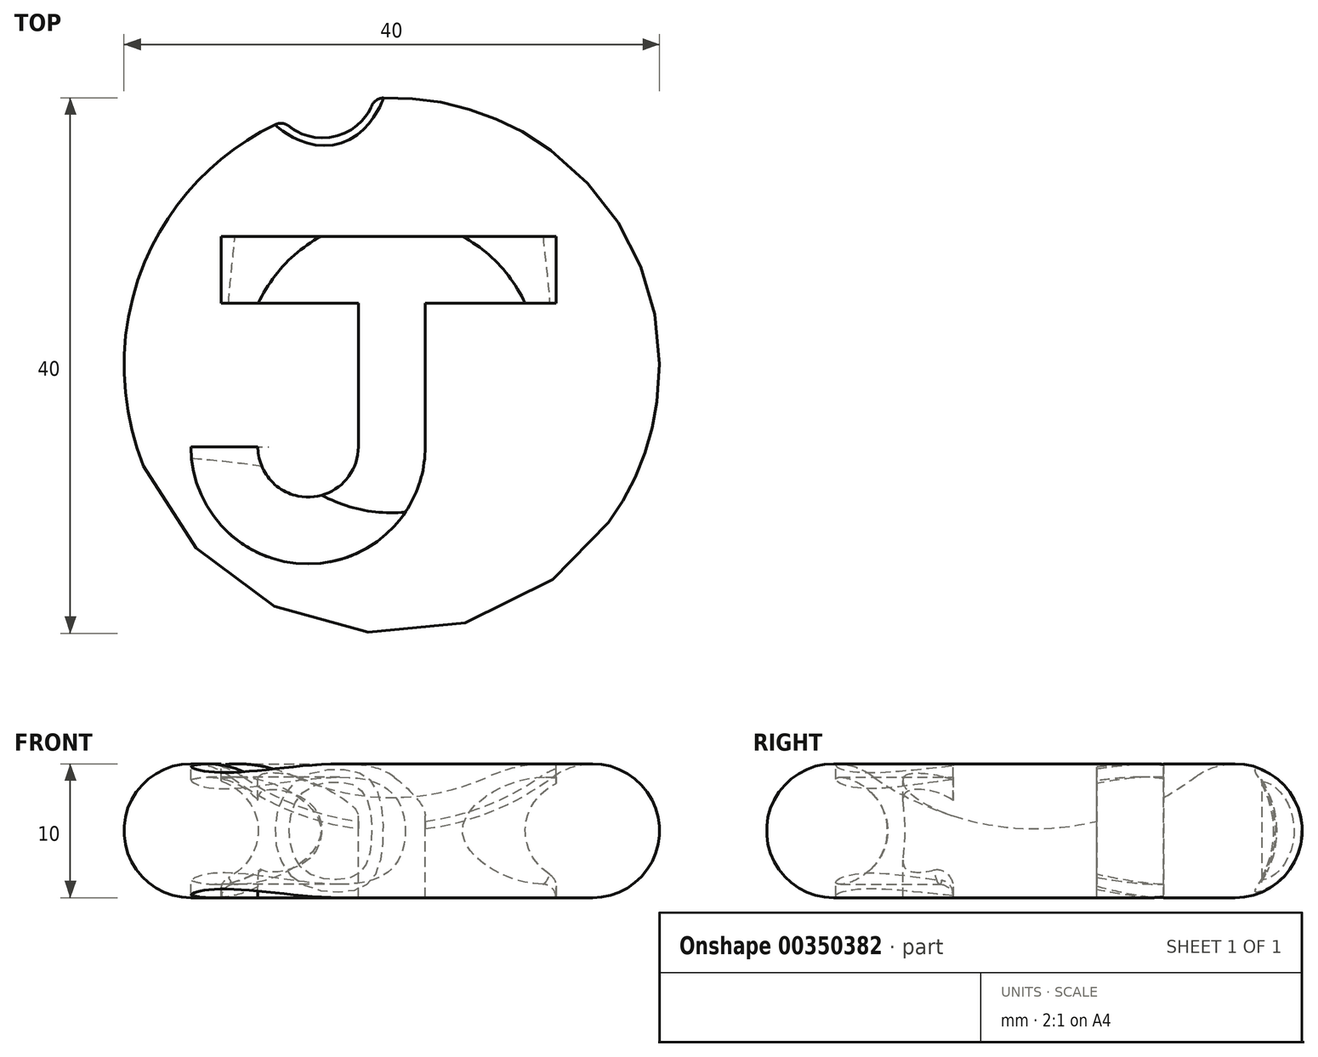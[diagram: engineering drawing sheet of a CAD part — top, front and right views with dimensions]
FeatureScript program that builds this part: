
annotation { "Feature Type Name" : "Feature", "Feature Type Description" : "" }
export const myFeature = defineFeature(function(context is Context, id is Id, definition is map)
    precondition{}
    {
        {
            var Q0;
            Q0=qCreatedBy(makeId("Front.planeOp"),FACE);
            var sketch = newSketch(context, id + "F0", { "sketchPlane" : qUnion([Q0])});
            skArc(sketch, "E0", {"start": v(-12, 9) * mm, "mid": v(-19.74, 6.58) * mm, "end": v(-15, 0) * mm});
            skArc(sketch, "E1", {"start": v(-12, 9) * mm, "mid": v(-6.32, 6.03) * mm, "end": v(0, 5) * mm});
            skLineSegment(sketch, "E2", {"start": v(-15, 0) * mm, "end": v(0, 0) * mm});
            skLineSegment(sketch, "E3", {"start": v(0, 0) * mm, "end": v(0, 5) * mm});
            skPoint(sketch, "E4.orphan", {"position": v(-50.33, 0) * mm});
            skSolve(sketch);
        }
        {
            var Q0;
            Q0=qCreatedBy(makeId("Top.planeOp"),FACE);
            cPlane(context, id + "F1", {"entities" : qUnion([Q0]), "cplaneType" : CPlaneType.OFFSET, "offset" : 10 * mm, "width" : 150 * mm, "height" : 150 * mm});
        }
        {
            var Q0;
            Q0=qCreatedBy(id+"F1.planeOp",FACE);
            var sketch = newSketch(context, id + "F2", { "sketchPlane" : qUnion([Q0])});
            skLineSegment(sketch, "E5", {"start": v(-12.74, 9.65) * mm, "end": v(12.26, 9.65) * mm});
            skLineSegment(sketch, "E6", {"start": v(-12.74, 4.65) * mm, "end": v(-2.5, 4.65) * mm});
            skArc(sketch, "E7", {"start": v(-15, -6.07) * mm, "mid": v(-6.25, -14.82) * mm, "end": v(2.5, -6.07) * mm});
            skLineSegment(sketch, "E8.0", {"start": v(2.5, 4.65) * mm, "end": v(2.5, -6.07) * mm});
            skLineSegment(sketch, "E9.0", {"start": v(-2.5, 4.65) * mm, "end": v(-2.5, -6.07) * mm});
            skLineSegment(sketch, "E10", {"start": v(-15, -6.07) * mm, "end": v(-10, -6.07) * mm});
            skArc(sketch, "E11", {"start": v(-10, -6.07) * mm, "mid": v(-6.25, -9.82) * mm, "end": v(-2.5, -6.07) * mm});
            skLineSegment(sketch, "E12.trimOffspring", {"start": v(2.5, 4.65) * mm, "end": v(12.26, 4.65) * mm});
            skLineSegment(sketch, "E13.trimOffspring", {"start": v(-2.5, -13.98) * mm, "end": v(-2.5, -14.03) * mm});
            skLineSegment(sketch, "E14.0", {"start": v(-12.74, 9.65) * mm, "end": v(-12.74, 4.65) * mm});
            skLineSegment(sketch, "E15.0", {"start": v(12.26, 9.65) * mm, "end": v(12.26, 4.65) * mm});
            skSolve(sketch);
        }
        {
            var Q0;
            Q0=qCreatedBy(makeId("Front.planeOp"),FACE);
            var sketch = newSketch(context, id + "F3", { "sketchPlane" : qUnion([Q0])});
            skCircle(sketch, "E16", {"center": v(-15, 5) * mm, "radius": 4 * mm});
            skSolve(sketch);
        }
        {
            var Q0;
            Q0=makeQuery(id+"F0.imprint","IMPRINT",FACE,{"disambiguationData":[TD([[makeQuery(id+"F0.imprint","IMPRINT",EDGE,{"derivedFrom":sQuery(id+"F0.wireOp",EDGE,"E0")}),1.0]])]});
            var Q1;
            Q1=sQuery(id+"F0.wireOp",EDGE,"E3");
            revolve(context, id + "F4", {"entities" : qUnion([Q0]), "axis" : qUnion([Q1]), "revolveType" : RevolveType.FULL});
        }
        {
            var Q0;
            Q0 = qSketchRegion(id + "F2", true);
            extrude(context, id + "F5", {"entities" : qUnion([Q0]), "operationType" : NewBodyOperationType.REMOVE, "oppositeDirection" : true, "depth" : 25 * mm});
        }
        {
            var Q0;
            Q0 = qSketchRegion(id + "F3", true);
            var Q1;
            Q1=sQuery(id+"F0.wireOp",EDGE,"E3");
            revolve(context, id + "F6", {"operationType" : NewBodyOperationType.ADD, "entities" : qUnion([Q0]), "axis" : qUnion([Q1]), "revolveType" : RevolveType.FULL});
        }
        {
            var Q0;
            Q0=qCreatedBy(id+"F1.planeOp",FACE);
            var sketch = newSketch(context, id + "F7", { "sketchPlane" : qUnion([Q0])});
            skCircle(sketch, "E17", {"center": v(-5.16, 21) * mm, "radius": 4 * mm});
            skSolve(sketch);
        }
        {
            var Q0;
            Q0 = qSketchRegion(id + "F7", true);
            var Q1;
            Q1=makeQuery(id+"F7.imprint","IMPRINT",FACE,{"disambiguationData":[TD([[makeQuery(id+"F7.imprint","IMPRINT",EDGE,{"derivedFrom":sQuery(id+"F7.wireOp",EDGE,"E17")}),1.0]])]});
            extrude(context, id + "F8", {"entities" : qUnion([Q0, Q1]), "operationType" : NewBodyOperationType.REMOVE, "oppositeDirection" : true, "depth" : 25 * mm});
        }
        {
            var Q0;
            Q0=makeQuery(id+"F8.boolean.opBoolean","INTERSECT",EDGE,{"derivedFrom":[makeQuery(id+"F5.boolean.opBoolean","SPLIT",FACE,{"disambiguationData":[TD([makeQuery(id+"F4.opRevolve","SWEPT_FACE",FACE,{"disambiguationData":[OSD([sQuery(id+"F0.wireOp",EDGE,"E2")])]})])],"derivedFrom":makeQuery(id+"F4.opRevolve","SWEPT_FACE",FACE,{"disambiguationData":[OSD([sQuery(id+"F0.wireOp",EDGE,"E0")])]})}),makeQuery(id+"F8.opExtrude","SWEPT_FACE",FACE,{"disambiguationData":[OSD([sQuery(id+"F7.wireOp",EDGE,"E17")])]})]});
            fillet(context, id + "F9", {"entities" : qUnion([Q0]), "radius" : 1 * mm, "tangentPropagation" : true, "allowEdgeOverflow" : false});
        }
        {
            var Q0;
            Q0=makeQuery(id+"F6.boolean.opBoolean","INTERSECT",EDGE,{"disambiguationData":[OD(0.0)],"derivedFrom":[makeQuery(id+"F5.boolean.opBoolean","COPY",FACE,{"derivedFrom":makeQuery(id+"F5.opExtrude","SWEPT_FACE",FACE,{"disambiguationData":[OSD([sQuery(id+"F2.wireOp",EDGE,"E14.0")])]})}),makeQuery(id+"F6.opRevolve","SWEPT_FACE",FACE,{"disambiguationData":[OSD([sQuery(id+"F3.wireOp",EDGE,"E16")])]})]});
            var Q1;
            Q1=makeQuery(id+"F6.boolean.opBoolean","INTERSECT",EDGE,{"disambiguationData":[OD(0.0)],"derivedFrom":[makeQuery(id+"F5.boolean.opBoolean","COPY",FACE,{"derivedFrom":makeQuery(id+"F5.opExtrude","SWEPT_FACE",FACE,{"disambiguationData":[OSD([sQuery(id+"F2.wireOp",EDGE,"E15.0")])]})}),makeQuery(id+"F6.opRevolve","SWEPT_FACE",FACE,{"disambiguationData":[OSD([sQuery(id+"F3.wireOp",EDGE,"E16")])]})]});
            var Q2;
            Q2=makeQuery(id+"F6.boolean.opBoolean","INTERSECT",EDGE,{"disambiguationData":[OD(1.0)],"derivedFrom":[makeQuery(id+"F5.boolean.opBoolean","COPY",FACE,{"derivedFrom":makeQuery(id+"F5.opExtrude","SWEPT_FACE",FACE,{"disambiguationData":[OSD([sQuery(id+"F2.wireOp",EDGE,"E10")])]})}),makeQuery(id+"F6.opRevolve","SWEPT_FACE",FACE,{"disambiguationData":[OSD([sQuery(id+"F3.wireOp",EDGE,"E16")])]})]});
            fillet(context, id + "F10", {"entities" : qUnion([Q0, Q1, Q2]), "radius" : 1 * mm, "tangentPropagation" : true, "allowEdgeOverflow" : false});
        }
    });
